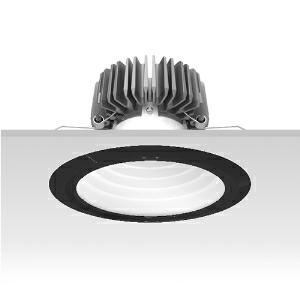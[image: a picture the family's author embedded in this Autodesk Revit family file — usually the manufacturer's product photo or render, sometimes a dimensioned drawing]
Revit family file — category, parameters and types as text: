
# Revit family: 3f_filippi_-_3f_reno_bianco_ampio_3f_filippi_-_30621_a01026_-_3f_reno_200_wh_2000-840_wide___vt_bk_2de3
name_source: partatom
category: Lighting Fixtures
units: mm (PartAtom-declared; Revit-internal decimal feet)

## family parameters
Cut with Voids When Loaded = No
Host = Face
Light Source = No
Part Type = Normal
Room Calculation Point = No
Round Connector Dimension = Use Diameter
Shared = No

## types (1)
- 3F Filippi - 3F Reno Bianco Ampio (1 x LED, 1884 lm, 20 W, 4000 K)
    Apparent Load = 20 VA
    Approval mark = CE
    CIE Flux Codes = 75 94 99 100 100
    Color Rendering = 80
    Color Temperature = 4000 K
    Control Gear = Electronic ballast
    Default Elevation = 1800 mm
    Description = ILLUMINOTECHNICAL
Luminous efficiency 100% (DLOR 100%, ULOR 0%).
Initial luminous flux of the luminaire 1884 lm.
Direct symmetric wide distribution.
Installation Interdistance Transv.D = 1.56 x hu - Long.D = 1.56 x hu.
Average luminance <3000 cd/m² for radial angles >65°.
Tabular UGR (CIE 117 - 4H-8H; S=0.25H; 70/50/20): RUG 20.8 - 20.6.
Beam angle: 74° - 74°.
Luminous efficacy 94 lm/W.
Lifetime (L90/B10): 30000 h. (tq+25°C)
Lifetime (L85/B10): 50000 h. (tq+25°C)
Lifetime (L70/B10): 80000 h. (tq+25°C)
Sudden decreased luminous flux after 50000 hours: 0% (C0).
Photobiological safety in compliance with IEC/TR 62778: RG0 risk exempt, (IEC 62471).
In compliance with IEC/EN 62722-2-1 - IEC/EN 62717 standards.

SOURCE
Compact LED module 2000/840.
Energy efficiency class (UE 2019/2020 - UE 2019/2015): D.
CIE 13.3 Colour rendering index: CRI >80 (R9 <50%).
IES TM-30 Fidelity Index: Rf = 84 Rg = 95.
CCT nominal colour temperature 4000 K.
Colour initial tolerance (MacAdam): SDCM 3.
Zhaga Book 3 compliant.

MECHANICAL
Passive heat dissipator in die-casting aluminium, oversized, for optimum thermal management of the LED module.
Parabolic element with graduated/concentric rings in white polycarbonate.
Transparent external lens with glossy and satin differentiated surfaces, with a cooling and anti-insect system in methacrylate (PMMA).
Fastening spring clips in stainless steel.
Dimensions: diameter 226 mm, height 146 mm. Weight 1.06 kg.
IP44 protection degree for exposed part, IP20 for recessed part.
Mechanical strength to impacts IK06 (1 joule).
Glow-wire test resistance 650°C.

ELECTRICAL
Wiring on a separate unit.
Halogen Free electronic wiring 230V-50/60Hz, power factor 0.95, THD <25%, constant output current, SELV, class II, 1 driver.
Power of the luminaire 20 W.
ENEC - CE.
SAFE FLICKER: PstLM=<1 and SVM=<0.4 (IEC TR 61547-1 and IEC TR 63158), to ensure a more comfortable and safe light.
Luminaire compliant with EN 60598-2-22 for power supply from a centralised emergency system CPSS (Central Power Supply System), not incorporated in the luminaire - high risk areas excluded. The default power and flux are 100% in AC and 100% in DC.
Ambient temperature from 0°C to +25°C.
Temperature class T6 max 85°C.
Relative humidity UR: <85%.

INSTALLATION
Pull-up recessed fitting.
False ceiling carving: 200 mm.
All accessories dedicated to this product are available on the Catalog and on our website www.3F-Filippi.com.

ACCESSORIES
A01026 - VT transparent glass, tempered, not flammable, locked and in line with the trim, in black polycarbonate.

APPLICATIONS
Environments: architectural, commercial, exhibition areas, transit areas, corridors, shops, display windows, service areas.
In false ceilings with narrow voids.

WARNING
Luminaire designed for disposal/recycling at end-of-life.
Replaceable (LED only) light source by a professional. Replaceable control gear by a professional.
    Height = 0 mm  [stored 0 ft]
    Lamp = 1 x LED
    Lamp Light Flux = 1884 lm
    Lamp Power = 20 W
    Lamp count = 1
    Length = 226 mm
    Lifetime = 50000 h
    Luminous efficacy = 94 lm/W
    Manufacturer = 3F Filippi
    ModVariant = No
    Model = 3F Filippi - 30621+A01026 - 3F Reno 200 WH 2000-840 WIDE + VT BK
    Mounting Place = Ceiling
    Mounting Type = Recessed
    Number of Poles = 1
    OnlyDefault = Yes
    Power Factor = 1
    Product Name = 3F Filippi - 3F Reno Bianco Ampio
    Product group = recessed luminaire
    ProductGroupID = 4
    Protection Class = Protection class II
    Protection Degree = IP 20
    RLX_Detail_Level = 1
    RLX_Emergency_Light_Flux = 0 lm
    RLX_Emergency_Type = 0
    RLX_Emergency_Type_DB = No
    RlxData = <blob elided: 100785 chars, md5=59945b1c>
    Socket = socket
    Standby Power = 0 W
    System Light Flux = 1884 lm
    System Power = 20 W
    Type Comments = Product without accessories
    Type Image = 3ffilippi_3f_reno_200_wh__a01026.jpg
    URL = http://relux.com
    VarID = ---
    Voltage = 0 V
    Weight = 0.00 kg
    Width = 0 mm  [stored 0 ft]

note: [stored X ft] marks values corroborated as IEEE doubles in the binary element streams (Revit-internal decimal feet)

## geometry (parser evidence)
native form markers: Blend x4, Sweep x10
no freeform markers — native parametric forms only
